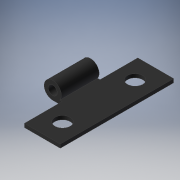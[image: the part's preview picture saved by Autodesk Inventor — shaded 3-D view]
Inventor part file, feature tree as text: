
AUTODESK INVENTOR PART (.ipt)
format: ipt  version: 2019 (Build 230136000, 136)  size: 139,776 bytes
history: native  units: mm
features: other x7, sketch x3, extrude x2, hole x1, pattern_linear x1
ambient origin geometry x8: Origin, YZ Plane, XZ Plane, XY Plane, X Axis, Y Axis, Z Axis, Center Point
bodies: Solid1 (feature_tree)
feature tree (14):
  extrude  "Extrusion1"  Depth=25.0mm TaperAngle=0.0deg
  extrude  "Extrusion2"  Depth=10.0mm TaperAngle=0.0deg
  hole  "Hole1"  [1 undecoded]
  pattern_linear  "Rectangular Pattern1"  [2 undecoded]
  other  "to_leaf2_XY"
  other  "to_leaf2_YZ"
  other  "to_leaf2_ZX"
  other  "to_leaf2_X"
  other  "to_leaf2_Y"
  other  "to_leaf2_Z"
  other  "to_leaf2_Center"
  sketch  "Sketch_15"
  sketch  "Sketch_1"  dims[d0=25.0mm d1=0.0mm d2=3.8mm d3=0.0mm]
  sketch  "Sketch3"  dims[d4=3.4mm d5=6.0mm d6=4.0mm d7=2.0mm d8=90.0deg d9=0.8mm d10=0.0mm d11=20.0mm d13=16.0mm d14=10.0mm d16=0.0mm]
note: 3 required parameter values undecoded (feature->parameter linkage not recoverable at this tier; creation-order binding heuristic only, values carry confidence <= 0.55)
